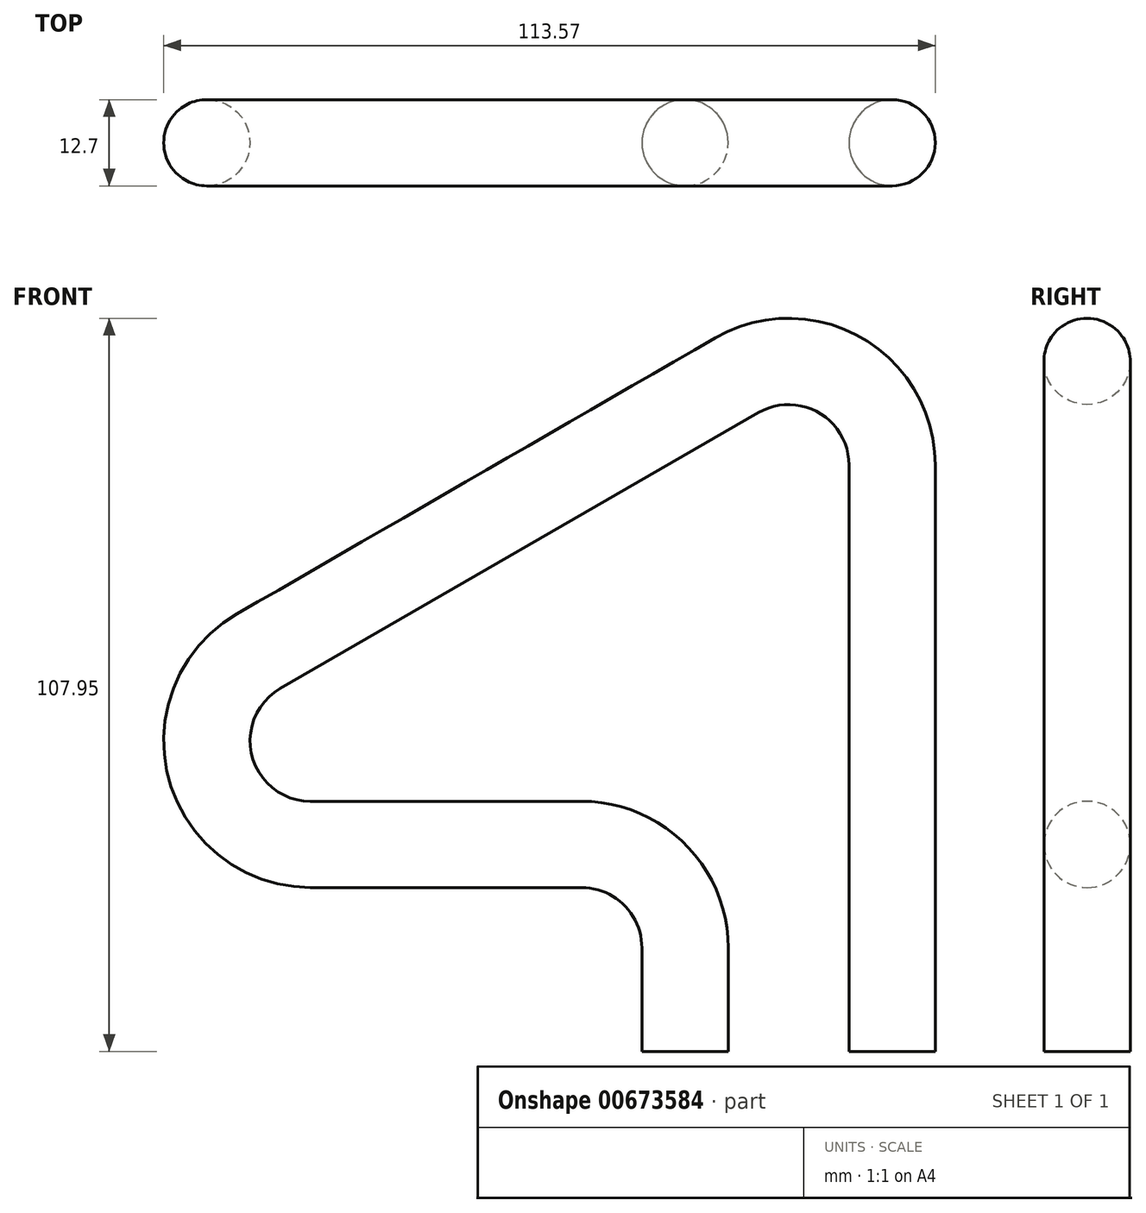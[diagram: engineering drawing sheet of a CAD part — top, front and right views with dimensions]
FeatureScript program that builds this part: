
annotation { "Feature Type Name" : "Feature", "Feature Type Description" : "" }
export const myFeature = defineFeature(function(context is Context, id is Id, definition is map)
    precondition{}
    {
        {
            var Q0;
            Q0=qCreatedBy(makeId("Front.planeOp"),FACE);
            var sketch = newSketch(context, id + "F0", { "sketchPlane" : qUnion([Q0])});
            skLineSegment(sketch, "E0", {"start": v(0, 0) * mm, "end": v(0, 86.36) * mm});
            skLineSegment(sketch, "E1", {"start": v(-22.86, 99.56) * mm, "end": v(-93.25, 58.92) * mm});
            skLineSegment(sketch, "E2", {"start": v(-85.63, 30.48) * mm, "end": v(-45.72, 30.48) * mm});
            skLineSegment(sketch, "E3", {"start": v(-30.48, 15.24) * mm, "end": v(-30.48, 0) * mm});
            skPoint(sketch, "E4.visualSharp", {"position": v(0, 112.76) * mm});
            skArc(sketch, "E4.filletArc", {"start": v(0, 86.36) * mm, "mid": v(-7.62, 99.56) * mm, "end": v(-22.86, 99.56) * mm});
            skPoint(sketch, "E5.visualSharp", {"position": v(-142.5, 30.48) * mm});
            skArc(sketch, "E5.filletArc", {"start": v(-93.25, 58.92) * mm, "mid": v(-100.35, 41.78) * mm, "end": v(-85.63, 30.48) * mm});
            skPoint(sketch, "E6.visualSharp", {"position": v(-30.48, 30.48) * mm});
            skArc(sketch, "E6.filletArc", {"start": v(-30.48, 15.24) * mm, "mid": v(-34.94, 26.02) * mm, "end": v(-45.72, 30.48) * mm});
            skLineSegment(sketch, "E7", {"start": v(-68.15, 101.6) * mm, "end": v(39.25, 101.6) * mm, "construction": true});
            skSolve(sketch);
        }
        {
            var Q0;
            Q0=sQuery(id+"F0.wireOp",VERTEX,"E0.start");
            var Q1;
            Q1=sQuery(id+"F0.wireOp",EDGE,"E0");
            cPlane(context, id + "F1", {"entities" : qUnion([Q0, Q1]), "cplaneType" : CPlaneType.LINE_POINT, "offset" : 25.4 * mm, "width" : 152.4 * mm, "height" : 152.4 * mm});
        }
        {
            var Q0;
            Q0=qCreatedBy(id+"F1.planeOp",FACE);
            var sketch = newSketch(context, id + "F2", { "sketchPlane" : qUnion([Q0])});
            skCircle(sketch, "E8", {"center": v(0, 0) * mm, "radius": 6.35 * mm});
            skSolve(sketch);
        }
        {
            var Q0;
            Q0=makeQuery(id+"F2.imprint","IMPRINT",FACE,{"disambiguationData":[TD([[makeQuery(id+"F2.imprint","IMPRINT",EDGE,{"derivedFrom":sQuery(id+"F2.wireOp",EDGE,"E8")}),1.0]])]});
            var Q1;
            Q1 = qConstructionFilter(qBodyType(qCreatedBy(id + "F0" ,EDGE), BodyType.WIRE), ConstructionObject.NO);
            sweep(context, id + "F3", {"profiles" : qUnion([Q0]), "path" : qUnion([Q1])});
        }
    });
